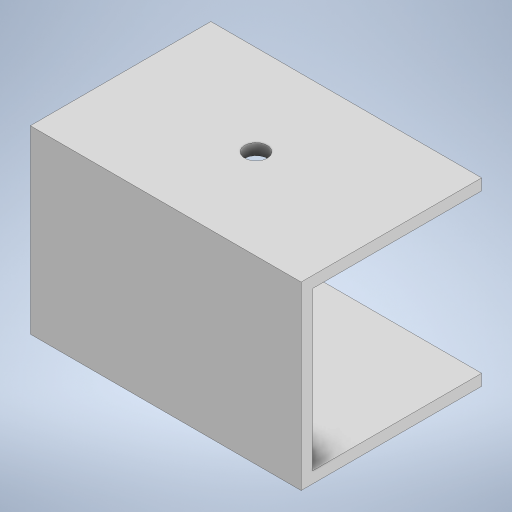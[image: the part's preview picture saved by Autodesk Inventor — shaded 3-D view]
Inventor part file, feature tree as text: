
AUTODESK INVENTOR PART (.ipt)
format: ipt  version: 2023 (Build 270158030, 158C)  size: 195,584 bytes
history: native  units: in
note: dims shown in document units (in); Inventor stores cm internally (conversion verified against a paired STEP export)
features: extrude x3, sketch x2
ambient origin geometry x8: Origin, YZ Plane, XZ Plane, XY Plane, X Axis, Y Axis, Z Axis, Center Point
bodies: Solid1 (feature_tree)
feature tree (5):
  sketch  "Sketch1"  dims[d0=3.0in d1=2.0in]
  extrude  "Extrusion1"  Depth=2.0in
  extrude  "Extrusion2"  Depth=0.125in TaperAngle=0.0deg
  extrude  "Extrusion3"  Depth=2.0in TaperAngle=0.0deg
  sketch  "Sketch2"  dims[d2=0.125in d3=0.125in d4=0.0in d5=2.0in d6=0.0in d7=0.125in d8=0.0in d9=0.25in d10=1.5in d11=1.0in d12=0.25in]
